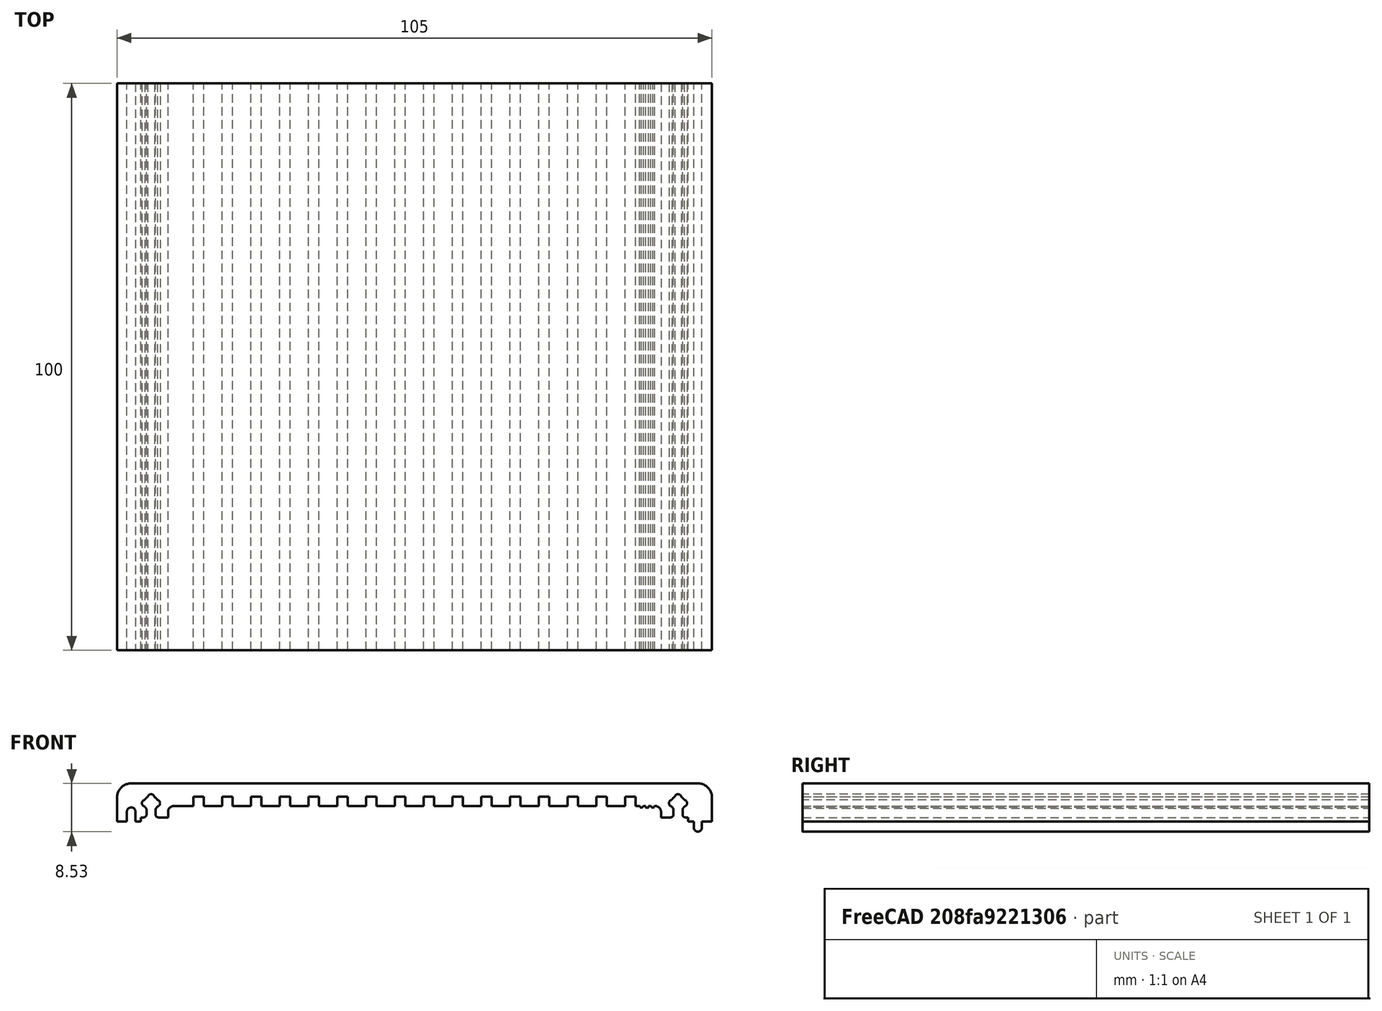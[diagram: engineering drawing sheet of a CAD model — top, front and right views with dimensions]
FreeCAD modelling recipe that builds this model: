
FCSTD DOCUMENT  (FreeCAD 0.19R24267 +99 (Git))
Label: KOH-0100
License: All rights reserved
LicenseURL: http://en.wikipedia.org/wiki/All_rights_reserved
objects: Part::FeaturePython×2, Part::Feature×1, Part::Compound×1, PartDesign::CoordinateSystem×1, PartDesign::Plane×1, App::Part×1
note: 6 computed .brp shape members not serialized (recipe doc carries the construction recipe); baked Part::Feature solids carry a one-line shape summary decoded from their .brp

FEATURE [Part::Feature] Part__Feature  label="KOH 0"
  Placement = pos=(0,0,0) rot=(-1,0,0;1.5708rad)
  shape: bbox 105 x 160 x 8.533 mm, 128 faces (baked)
FEATURE [Part::Compound] Compound
  Links = -> [Part__Feature]
FEATURE [PartDesign::CoordinateSystem] LCS_0  label="LCS_KOH0100_CornerTop"
  AttacherType = Attacher::AttachEngine3D
  MapMode = 2
  Support = -> [X_Axis]
FEATURE [PartDesign::Plane] Offset
  AttachmentOffset = pos=(0,0,100) rot=(0,0,1;0rad)
  Length = 100
  MapMode = 5
  Placement = pos=(0,100,2.22e-14) rot=(0,0.707107,0.707107;3.14159rad)
  ResizeMode = 1
  Support = -> [XZ_Plane]
  Width = 100
FEATURE [Part::FeaturePython] Slice  # WARN: FeaturePython — macro-defined, semantics opaque (R4)
  Base = -> Compound
  Mode = 1
  Tolerance = 0
  Tools = -> [Offset]
FEATURE [Part::FeaturePython] Slice_child0  label="Slice.0"  # WARN: FeaturePython — macro-defined, semantics opaque (R4)
  Base = -> Slice
  FilterType = 1
  Invert = false
  OverrideMaxVal = 0
  WindowFrom = 80
  WindowTo = 100
  items = 0
FEATURE [App::Part] KOH_0100
  Group = -> [LCS_0,Part__Feature,Compound,Offset,Slice,Slice_child0]
  Origin = -> Origin
